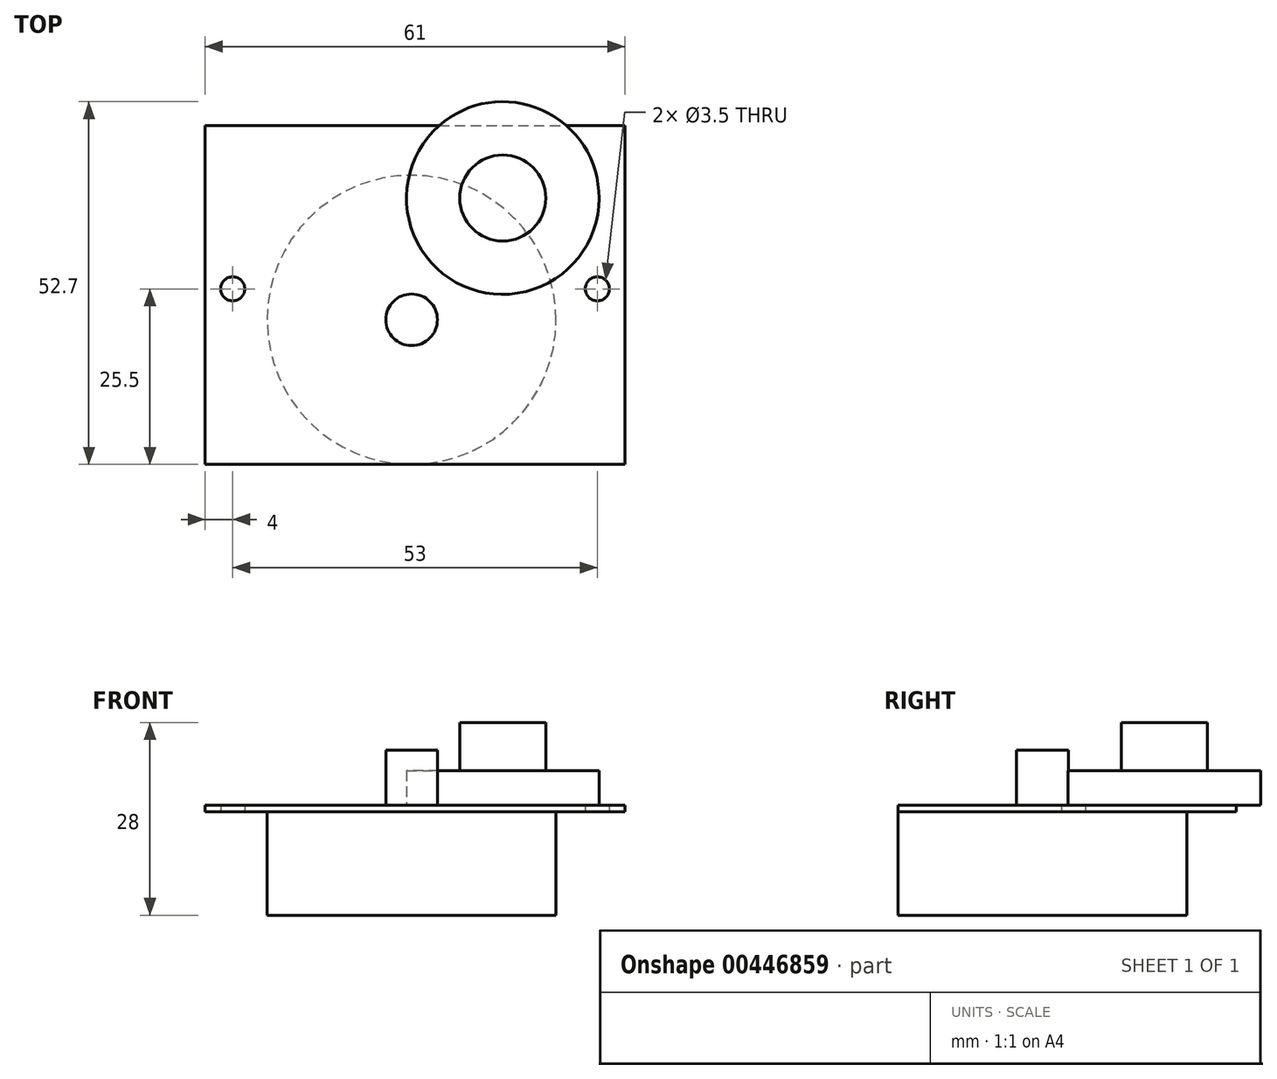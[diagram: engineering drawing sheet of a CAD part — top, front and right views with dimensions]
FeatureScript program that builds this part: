
annotation { "Feature Type Name" : "Feature", "Feature Type Description" : "" }
export const myFeature = defineFeature(function(context is Context, id is Id, definition is map)
    precondition{}
    {
        {
            var Q0;
            Q0=qCreatedBy(makeId("Top.planeOp"),FACE);
            var sketch = newSketch(context, id + "F0", { "sketchPlane" : qUnion([Q0])});
            skLineSegment(sketch, "E0.bottom", {"start": v(0, 0) * mm, "end": v(61, 0) * mm});
            skLineSegment(sketch, "E0.top", {"start": v(0, 49.2) * mm, "end": v(61, 49.2) * mm});
            skLineSegment(sketch, "E0.left", {"start": v(0, 0) * mm, "end": v(0, 49.2) * mm});
            skLineSegment(sketch, "E0.right", {"start": v(61, 0) * mm, "end": v(61, 49.2) * mm});
            skPoint(sketch, "E1", {"position": v(4, 25.5) * mm});
            skPoint(sketch, "E2", {"position": v(57, 25.5) * mm});
            skSolve(sketch);
        }
        {
            var Q0;
            Q0=makeQuery(id+"F0.imprint","IMPRINT",FACE,{"disambiguationData":[TD([[makeQuery(id+"F0.imprint","IMPRINT",EDGE,{"derivedFrom":sQuery(id+"F0.wireOp",EDGE,"E0.bottom")}),1.0]])]});
            extrude(context, id + "F1", {"entities" : qUnion([Q0]), "depth" : 1 * mm});
        }
        {
            var Q0;
            Q0=sQuery(id+"F0.wireOp",VERTEX,"E1");
            var Q1;
            Q1=sQuery(id+"F0.wireOp",VERTEX,"E2");
            var Q2;
            Q2=makeQuery(id+"F1.opExtrude","SWEPT_BODY",BODY,{"disambiguationData":[OSD([sQuery(id+"F0.wireOp",EDGE,"E0.bottom"),sQuery(id+"F0.wireOp",EDGE,"E0.top"),sQuery(id+"F0.wireOp",EDGE,"E0.left"),sQuery(id+"F0.wireOp",EDGE,"E0.right")])]});
            hole(context, id + "F2", {"style" : HoleStyle.SIMPLE, "endStyle" : HoleEndStyle.THROUGH, "oppositeDirection" : true, "holeDiameter" : 3.5 * mm, "isTappedThrough" : true, "tappedDepth" : 12 * mm, "tapClearance" : 3, "locations" : qUnion([Q0, Q1]), "scope" : qUnion([Q2])});
        }
        {
            var Q0;
            Q0=makeQuery(id+"F1.opExtrude","CAP_FACE",FACE,{"disambiguationData":[OSD([sQuery(id+"F0.wireOp",EDGE,"E0.bottom"),sQuery(id+"F0.wireOp",EDGE,"E0.top"),sQuery(id+"F0.wireOp",EDGE,"E0.left"),sQuery(id+"F0.wireOp",EDGE,"E0.right")])],"isStart":false});
            var sketch = newSketch(context, id + "F3", { "sketchPlane" : qUnion([Q0])});
            skCircle(sketch, "E3", {"center": v(30, 21) * mm, "radius": 3.75 * mm});
            skCircle(sketch, "E4", {"center": v(43.25, 21) * mm, "radius": 9.5 * mm});
            skCircle(sketch, "E5", {"center": v(43.25, 38.7) * mm, "radius": 14 * mm});
            skCircle(sketch, "E6", {"center": v(43.25, 38.7) * mm, "radius": 6.25 * mm});
            skSolve(sketch);
        }
        {
            var Q0;
            Q0=makeQuery(id+"F3.imprint","IMPRINT",FACE,{"disambiguationData":[TD([[makeQuery(id+"F3.imprint","IMPRINT",EDGE,{"derivedFrom":sQuery(id+"F3.wireOp",EDGE,"E3")}),1.0]])]});
            extrude(context, id + "F4", {"entities" : qUnion([Q0]), "operationType" : NewBodyOperationType.ADD, "depth" : 8 * mm});
        }
        {
            var Q0;
            {var subQ0=sQuery(id+"F3.wireOp",EDGE,"E5");var subQ1=makeQuery(id+"F1.opExtrude","CAP_EDGE",EDGE,{"disambiguationData":[OSD([sQuery(id+"F0.wireOp",EDGE,"E0.top")])],"isStart":false});var subQ2=makeQuery(id+"F3.imprint","INTERSECT",VERTEX,{"disambiguationData":[OD(0.0)],"derivedFrom":[subQ1,subQ0]});Q0=makeQuery(id+"F3.imprint","IMPRINT",FACE,{"disambiguationData":[TD([[makeQuery(id+"F3.imprint","IMPRINT",EDGE,{"disambiguationData":[TD([[subQ2,1.0]])],"derivedFrom":subQ0}),1.0]])]});}
            var Q1;
            Q1=makeQuery(id+"F3.imprint","IMPRINT",FACE,{"disambiguationData":[TD([[makeQuery(id+"F3.imprint","IMPRINT",EDGE,{"derivedFrom":sQuery(id+"F3.wireOp",EDGE,"E6")}),-1.0]])]});
            var Q2;
            Q2=makeQuery(id+"F3.imprint","IMPRINT",FACE,{"disambiguationData":[TD([[makeQuery(id+"F3.imprint","IMPRINT",EDGE,{"derivedFrom":sQuery(id+"F3.wireOp",EDGE,"E6")}),1.0]])]});
            var Q3;
            {var subQ0=sQuery(id+"F3.wireOp",EDGE,"E5");var subQ1=sQuery(id+"F3.wireOp",EDGE,"E4");var subQ2=makeQuery(id+"F3.imprint","INTERSECT",VERTEX,{"disambiguationData":[OD(0.0)],"derivedFrom":[subQ1,subQ0]});Q3=makeQuery(id+"F3.imprint","IMPRINT",FACE,{"disambiguationData":[TD([[makeQuery(id+"F3.imprint","IMPRINT",EDGE,{"disambiguationData":[TD([[subQ2,1.0]])],"derivedFrom":subQ1}),1.0]])]});}
            var Q4;
            Q4=sQuery(id+"F3.wireOp",EDGE,"E5");
            extrude(context, id + "F5", {"entities" : qUnion([Q0, Q1, Q2, Q3]), "operationType" : NewBodyOperationType.ADD, "surfaceEntities" : qUnion([Q4]), "depth" : 5 * mm});
        }
        {
            var Q0;
            Q0=makeQuery(id+"F0.imprint","IMPRINT",FACE,{"disambiguationData":[TD([[makeQuery(id+"F0.imprint","IMPRINT",EDGE,{"derivedFrom":sQuery(id+"F0.wireOp",EDGE,"E0.bottom")}),1.0]])]});
            var sketch = newSketch(context, id + "F6", { "sketchPlane" : qUnion([Q0])});
            skPoint(sketch, "E7.0", {"position": v(30, 21) * mm});
            skCircle(sketch, "E8", {"center": v(30, 21) * mm, "radius": 21 * mm});
            skSolve(sketch);
        }
        {
            var Q0;
            Q0 = qSketchRegion(id + "F6", true);
            extrude(context, id + "F7", {"entities" : qUnion([Q0]), "operationType" : NewBodyOperationType.ADD, "oppositeDirection" : true, "depth" : 15 * mm});
        }
        {
            var Q0;
            Q0=makeQuery(id+"F5.opExtrude","CAP_FACE",FACE,{"disambiguationData":[OSD([sQuery(id+"F3.wireOp",EDGE,"E5")])],"isStart":false});
            var sketch = newSketch(context, id + "F8", { "sketchPlane" : qUnion([Q0])});
            skPoint(sketch, "E9.0", {"position": v(43.25, 38.7) * mm});
            skCircle(sketch, "E10.0", {"center": v(43.25, 38.7) * mm, "radius": 6.25 * mm});
            skSolve(sketch);
        }
        {
            var Q0;
            Q0 = qSketchRegion(id + "F8", true);
            extrude(context, id + "F9", {"entities" : qUnion([Q0]), "operationType" : NewBodyOperationType.ADD, "depth" : 7 * mm});
        }
    });
